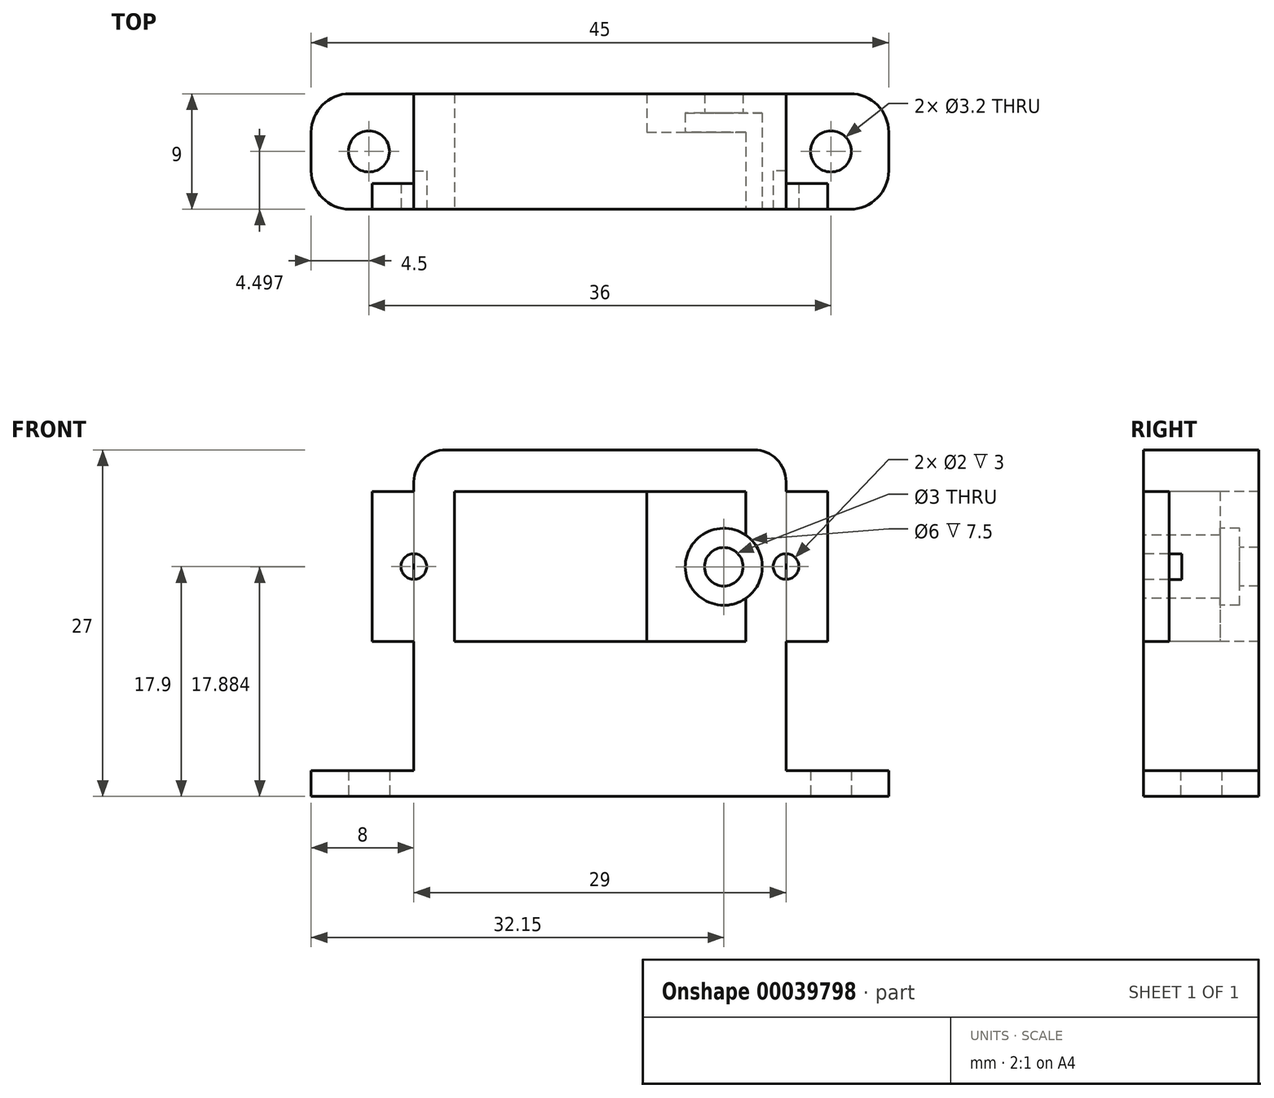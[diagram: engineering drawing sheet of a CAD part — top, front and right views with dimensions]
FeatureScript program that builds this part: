
annotation { "Feature Type Name" : "Feature", "Feature Type Description" : "" }
export const myFeature = defineFeature(function(context is Context, id is Id, definition is map)
    precondition{}
    {
        {
            var Q0;
            Q0=qCreatedBy(makeId("Top.planeOp"),FACE);
            var sketch = newSketch(context, id + "F0", { "sketchPlane" : qUnion([Q0])});
            skLineSegment(sketch, "E0.bottom", {"start": v(-18.83, 3.33) * mm, "end": v(26.17, 3.33) * mm});
            skLineSegment(sketch, "E0.top", {"start": v(-18.83, -5.67) * mm, "end": v(26.17, -5.67) * mm});
            skLineSegment(sketch, "E0.left", {"start": v(-18.83, 3.33) * mm, "end": v(-18.83, -5.67) * mm});
            skLineSegment(sketch, "E0.right", {"start": v(26.17, 3.33) * mm, "end": v(26.17, -5.67) * mm});
            skCircle(sketch, "E1", {"center": v(-14.33, -1.17) * mm, "radius": 1.6 * mm});
            skCircle(sketch, "E2", {"center": v(21.67, -1.17) * mm, "radius": 1.6 * mm});
            skLineSegment(sketch, "E3", {"start": v(-10.83, 3.33) * mm, "end": v(-10.83, -5.67) * mm});
            skLineSegment(sketch, "E4", {"start": v(18.17, 3.33) * mm, "end": v(18.17, -5.67) * mm});
            skSolve(sketch);
        }
        {
            var Q0;
            {var subQ1=sQuery(id+"F0.wireOp",EDGE,"E3");Q0=makeQuery(id+"F0.imprint","IMPRINT",FACE,{"disambiguationData":[TD([[makeQuery(id+"F0.imprint","IMPRINT",EDGE,{"derivedFrom":subQ1}),1.0]])]});}
            extrude(context, id + "F1", {"entities" : qUnion([Q0]), "depth" : 27 * mm});
        }
        {
            var Q0;
            {var subQ2=sQuery(id+"F0.wireOp",EDGE,"E0.left");Q0=makeQuery(id+"F0.imprint","IMPRINT",FACE,{"disambiguationData":[TD([[makeQuery(id+"F0.imprint","IMPRINT",EDGE,{"derivedFrom":subQ2}),1.0]])]});}
            var Q1;
            {var subQ2=sQuery(id+"F0.wireOp",EDGE,"E0.right");Q1=makeQuery(id+"F0.imprint","IMPRINT",FACE,{"disambiguationData":[TD([[makeQuery(id+"F0.imprint","IMPRINT",EDGE,{"derivedFrom":subQ2}),-1.0]])]});}
            extrude(context, id + "F2", {"entities" : qUnion([Q0, Q1]), "operationType" : NewBodyOperationType.ADD, "depth" : 2 * mm});
        }
        {
            var Q0;
            {var subQ0=sQuery(id+"F0.wireOp",EDGE,"E0.top");Q0=makeQuery(id+"F2.boolean.opBoolean","MERGE",FACE,{"derivedFrom":[makeQuery(id+"F1.opExtrude","SWEPT_FACE",FACE,{"disambiguationData":[OSD([subQ0])]}),makeQuery(id+"F2.opExtrude","SWEPT_FACE",FACE,{"disambiguationData":[OSD([subQ0]),TDD([makeQuery(id+"F0.imprint","IMPRINT",EDGE,{"disambiguationData":[TD([[makeQuery(id+"F0.imprint","INTERSECT",VERTEX,{"derivedFrom":[subQ0,sQuery(id+"F0.wireOp",EDGE,"E0.left")]}),-1.0]])],"derivedFrom":subQ0})])]}),makeQuery(id+"F2.opExtrude","SWEPT_FACE",FACE,{"disambiguationData":[OSD([subQ0]),TDD([makeQuery(id+"F0.imprint","IMPRINT",EDGE,{"disambiguationData":[TD([[makeQuery(id+"F0.imprint","INTERSECT",VERTEX,{"derivedFrom":[subQ0,sQuery(id+"F0.wireOp",EDGE,"E0.right")]}),1.0]])],"derivedFrom":subQ0})])]})]});}
            var sketch = newSketch(context, id + "F3", { "sketchPlane" : qUnion([Q0])});
            skLineSegment(sketch, "E5.bottom", {"start": v(-7.68, 23.75) * mm, "end": v(15.02, 23.75) * mm});
            skLineSegment(sketch, "E5.top", {"start": v(-7.68, 12.05) * mm, "end": v(15.02, 12.05) * mm});
            skLineSegment(sketch, "E5.left", {"start": v(-7.68, 23.75) * mm, "end": v(-7.68, 12.05) * mm});
            skLineSegment(sketch, "E5.right", {"start": v(15.02, 23.75) * mm, "end": v(15.02, 12.05) * mm});
            skLineSegment(sketch, "E6", {"start": v(7.32, 23.75) * mm, "end": v(7.32, 12.05) * mm});
            skCircle(sketch, "E7", {"center": v(13.32, 17.88) * mm, "radius": 1.5 * mm});
            skCircle(sketch, "E8", {"center": v(13.32, 17.88) * mm, "radius": 3 * mm});
            skSolve(sketch);
        }
        {
            var Q0;
            Q0=makeQuery(id+"F3.imprint","IMPRINT",FACE,{"disambiguationData":[TD([[makeQuery(id+"F3.imprint","IMPRINT",EDGE,{"derivedFrom":sQuery(id+"F3.wireOp",EDGE,"E5.bottom")}),-1.0]])]});
            var Q1;
            Q1=makeQuery(id+"F3.imprint","IMPRINT",FACE,{"disambiguationData":[TD([[makeQuery(id+"F3.imprint","IMPRINT",EDGE,{"derivedFrom":sQuery(id+"F3.wireOp",EDGE,"E7")}),1.0]])]});
            extrude(context, id + "F4", {"entities" : qUnion([Q0, Q1]), "operationType" : NewBodyOperationType.REMOVE, "oppositeDirection" : true, "depth" : 10 * mm});
        }
        {
            var Q0;
            {var subQ4=sQuery(id+"F3.wireOp",EDGE,"E6");Q0=makeQuery(id+"F3.imprint","IMPRINT",FACE,{"disambiguationData":[TD([[makeQuery(id+"F3.imprint","IMPRINT",EDGE,{"derivedFrom":subQ4}),1.0]])]});}
            extrude(context, id + "F5", {"entities" : qUnion([Q0]), "operationType" : NewBodyOperationType.REMOVE, "oppositeDirection" : true, "depth" : 6 * mm});
        }
        {
            var Q0;
            {var subQ4=sQuery(id+"F3.wireOp",EDGE,"E7");Q0=makeQuery(id+"F3.imprint","IMPRINT",FACE,{"disambiguationData":[TD([[makeQuery(id+"F3.imprint","IMPRINT",EDGE,{"derivedFrom":subQ4}),-1.0]])]});}
            var Q1;
            {var subQ0=sQuery(id+"F3.wireOp",EDGE,"E5.right");var subQ3=makeQuery(id+"F3.imprint","INTERSECT",VERTEX,{"derivedFrom":[subQ0,sQuery(id+"F3.wireOp",EDGE,"E7")]});Q1=makeQuery(id+"F3.imprint","IMPRINT",FACE,{"disambiguationData":[TD([[makeQuery(id+"F3.imprint","IMPRINT",EDGE,{"disambiguationData":[TD([[subQ3,1.0]])],"derivedFrom":subQ0}),1.0]])]});}
            extrude(context, id + "F6", {"entities" : qUnion([Q0, Q1]), "operationType" : NewBodyOperationType.REMOVE, "oppositeDirection" : true, "depth" : 7.5 * mm});
        }
        {
            var Q0;
            Q0=makeQuery(id+"F1.opExtrude","CAP_EDGE",EDGE,{"disambiguationData":[OSD([sQuery(id+"F0.wireOp",EDGE,"E3")])],"isStart":false});
            var Q1;
            Q1=makeQuery(id+"F1.opExtrude","CAP_EDGE",EDGE,{"disambiguationData":[OSD([sQuery(id+"F0.wireOp",EDGE,"E4")])],"isStart":false});
            fillet(context, id + "F7", {"entities" : qUnion([Q0, Q1]), "radius" : 2.5 * mm, "tangentPropagation" : true, "allowEdgeOverflow" : false});
        }
        {
            var Q0;
            Q0=makeQuery(id+"F2.opExtrude","SWEPT_EDGE",EDGE,{"disambiguationData":[OSD([sQuery(id+"F0.wireOp",EDGE,"E0.bottom"),sQuery(id+"F0.wireOp",EDGE,"E0.left")])]});
            var Q1;
            Q1=makeQuery(id+"F2.opExtrude","SWEPT_EDGE",EDGE,{"disambiguationData":[OSD([sQuery(id+"F0.wireOp",EDGE,"E0.top"),sQuery(id+"F0.wireOp",EDGE,"E0.left")])]});
            var Q2;
            Q2=makeQuery(id+"F2.opExtrude","SWEPT_EDGE",EDGE,{"disambiguationData":[OSD([sQuery(id+"F0.wireOp",EDGE,"E0.top"),sQuery(id+"F0.wireOp",EDGE,"E0.right")])]});
            var Q3;
            Q3=makeQuery(id+"F2.opExtrude","SWEPT_EDGE",EDGE,{"disambiguationData":[OSD([sQuery(id+"F0.wireOp",EDGE,"E0.bottom"),sQuery(id+"F0.wireOp",EDGE,"E0.right")])]});
            fillet(context, id + "F8", {"entities" : qUnion([Q0, Q1, Q2, Q3]), "radius" : 3 * mm, "tangentPropagation" : true, "allowEdgeOverflow" : false});
        }
        {
            var Q0;
            {var subQ0=sQuery(id+"F0.wireOp",EDGE,"E0.top");Q0=makeQuery(id+"F2.boolean.opBoolean","MERGE",FACE,{"derivedFrom":[makeQuery(id+"F1.opExtrude","SWEPT_FACE",FACE,{"disambiguationData":[OSD([subQ0])]}),makeQuery(id+"F2.opExtrude","SWEPT_FACE",FACE,{"disambiguationData":[OSD([subQ0]),TDD([makeQuery(id+"F0.imprint","IMPRINT",EDGE,{"disambiguationData":[TD([[makeQuery(id+"F0.imprint","INTERSECT",VERTEX,{"derivedFrom":[subQ0,sQuery(id+"F0.wireOp",EDGE,"E0.left")]}),-1.0]])],"derivedFrom":subQ0})])]}),makeQuery(id+"F2.opExtrude","SWEPT_FACE",FACE,{"disambiguationData":[OSD([subQ0]),TDD([makeQuery(id+"F0.imprint","IMPRINT",EDGE,{"disambiguationData":[TD([[makeQuery(id+"F0.imprint","INTERSECT",VERTEX,{"derivedFrom":[subQ0,sQuery(id+"F0.wireOp",EDGE,"E0.right")]}),1.0]])],"derivedFrom":subQ0})])]})]});}
            var sketch = newSketch(context, id + "F9", { "sketchPlane" : qUnion([Q0])});
            skLineSegment(sketch, "E9.bottom", {"start": v(-10.83, 12.05) * mm, "end": v(-14.08, 12.05) * mm});
            skLineSegment(sketch, "E9.top", {"start": v(-10.83, 23.75) * mm, "end": v(-14.08, 23.75) * mm});
            skLineSegment(sketch, "E9.left", {"start": v(-10.83, 12.05) * mm, "end": v(-10.83, 23.75) * mm});
            skLineSegment(sketch, "E9.right", {"start": v(-14.08, 12.05) * mm, "end": v(-14.08, 23.75) * mm});
            skLineSegment(sketch, "E10.bottom", {"start": v(18.17, 23.75) * mm, "end": v(21.42, 23.75) * mm});
            skLineSegment(sketch, "E10.top", {"start": v(18.17, 12.05) * mm, "end": v(21.42, 12.05) * mm});
            skLineSegment(sketch, "E10.left", {"start": v(18.17, 23.75) * mm, "end": v(18.17, 12.05) * mm});
            skLineSegment(sketch, "E10.right", {"start": v(21.42, 23.75) * mm, "end": v(21.42, 12.05) * mm});
            skCircle(sketch, "E11", {"center": v(-10.83, 17.9) * mm, "radius": 1.36 * mm, "construction": true});
            skCircle(sketch, "E12", {"center": v(-10.83, 17.9) * mm, "radius": 1 * mm});
            skCircle(sketch, "E13", {"center": v(18.17, 17.9) * mm, "radius": 1 * mm});
            skSolve(sketch);
        }
        {
            var Q0;
            {var subQ4=sQuery(id+"F9.wireOp",EDGE,"E9.bottom");Q0=makeQuery(id+"F9.imprint","IMPRINT",FACE,{"disambiguationData":[TD([[makeQuery(id+"F9.imprint","IMPRINT",EDGE,{"derivedFrom":subQ4}),-1.0]])]});}
            var Q1;
            {var subQ5=sQuery(id+"F9.wireOp",EDGE,"E10.bottom");Q1=makeQuery(id+"F9.imprint","IMPRINT",FACE,{"disambiguationData":[TD([[makeQuery(id+"F9.imprint","IMPRINT",EDGE,{"derivedFrom":subQ5}),-1.0]])]});}
            extrude(context, id + "F10", {"entities" : qUnion([Q0, Q1]), "operationType" : NewBodyOperationType.ADD, "oppositeDirection" : true, "depth" : 2 * mm});
        }
        {
            var Q0;
            {var subQ0=sQuery(id+"F9.wireOp",EDGE,"E12");var subQ1=sQuery(id+"F9.wireOp",EDGE,"E9.left");var subQ3=makeQuery(id+"F9.imprint","INTERSECT",VERTEX,{"disambiguationData":[OD(0.0)],"derivedFrom":[subQ1,subQ0]});Q0=makeQuery(id+"F9.imprint","IMPRINT",FACE,{"disambiguationData":[TD([[makeQuery(id+"F9.imprint","IMPRINT",EDGE,{"disambiguationData":[TD([[subQ3,-1.0]])],"derivedFrom":subQ1}),1.0]])]});}
            var Q1;
            {var subQ0=sQuery(id+"F9.wireOp",EDGE,"E13");var subQ1=sQuery(id+"F9.wireOp",EDGE,"E10.left");var subQ3=makeQuery(id+"F9.imprint","INTERSECT",VERTEX,{"disambiguationData":[OD(0.0)],"derivedFrom":[subQ1,subQ0]});Q1=makeQuery(id+"F9.imprint","IMPRINT",FACE,{"disambiguationData":[TD([[makeQuery(id+"F9.imprint","IMPRINT",EDGE,{"disambiguationData":[TD([[subQ3,-1.0]])],"derivedFrom":subQ1}),-1.0]])]});}
            extrude(context, id + "F11", {"entities" : qUnion([Q0, Q1]), "operationType" : NewBodyOperationType.REMOVE, "oppositeDirection" : true, "depth" : 3 * mm});
        }
    });
